# Revit family: 9580034
name_source: partatom
category: Equipamento especial
revit_build: Autodesk Revit 2016 (Build: 20150220_1215(x64)
units: mm (PartAtom-declared; Revit-internal decimal feet)

## family parameters
Compartilhado = Não
Corte com vazios quando carregados = Não
Cota do conector redondo = Utilizar diâmetro
Hospedeiro = Parede
Número OmniClass = 23.40.40.14.17.11
Ponto de cálculo do ambiente = Não
Sempre na vertical = Sim
Tipo de parte = Normal
Título OmniClass = Cookers, Ovens, Stoves

## types (1)
- Coifa Drita White - 9580034
    Atendimento ao Cliente = http://www.tramontina.com.br
    Classe da Construção = CLASSE I
    Código da Peça = Coifa Drita White - 9580034
    Descrição = Coifa Drita White - 9580034
    Desenvolvedor da Biblioteca = Factory Cursos e Desenvolvimento
    Dimensoes (mm) = 500x 900x  540-1020
    Disjuntor Termomagnético = 10 A
    Fabricante = Tramontina
    Filtro de Aluminio = 3
    Filtro de Carvao Ativado = 2
    Frequência = 60 Hz
    Grau de Proteção = IPXO
    Iluminação = 2 x 1,5 W - 12 V - Lâmpadas LED
    Linha = Dritta
    Modelo = Coifa Drita White - 9580034
    Numero de Velocidades = 3
    Nível de Ruído = 64 dB (A) - cfe. Norma EN 60704
    Peso Bruto (Kg) = 19.8
    Peso Líquido (Kg) = 16.7
    Potência Elétrica = 225 W
    Potência do Motor = 220 W
    Produto = Coifa Drita White - 9580034
    Segmento = Residencial
    Site do Desenvolvedor = www.factorycursos.com.br
    Tensão = 220 V
    URL = www.tramontina.com.br
    Vazão Máxima = 620 m³/h - cfe. Norma IEC 61591

## geometry (parser evidence)
native form markers: Sweep x2
no freeform markers — native parametric forms only
